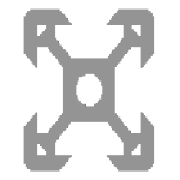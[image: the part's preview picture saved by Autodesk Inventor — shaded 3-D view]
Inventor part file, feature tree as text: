
AUTODESK INVENTOR PART (.ipt)
format: ipt  version: 2019 (Build 230136000, 136)  size: 198,656 bytes
history: native  units: mm
features: other x3, sketch x3, plane x1
ambient origin geometry x8: Origin, YZ Plane, XZ Plane, XY Plane, X Axis, Y Axis, Z Axis, Center Point
bodies: Solid1 (feature_tree), Body (feature_tree)
feature tree (7):
  other  "Driven Length"
  other  "Start Plane"
  other  "End Plane"
  sketch  "Sketch1"  dims[d2=4.2mm]
  sketch  "Sketch4"  dims[d3=1.5mm]
  plane  "Work Plane4"
  sketch  "Sketch5"  dims[d4=1.64mm d5=1.8mm d6=5.68mm d7=1.8mm d9=1.5mm d12=-0.0mm d13=340.0mm d14=0.13mm d15=0.0mm d18=90.0deg d17=340.0mm]
